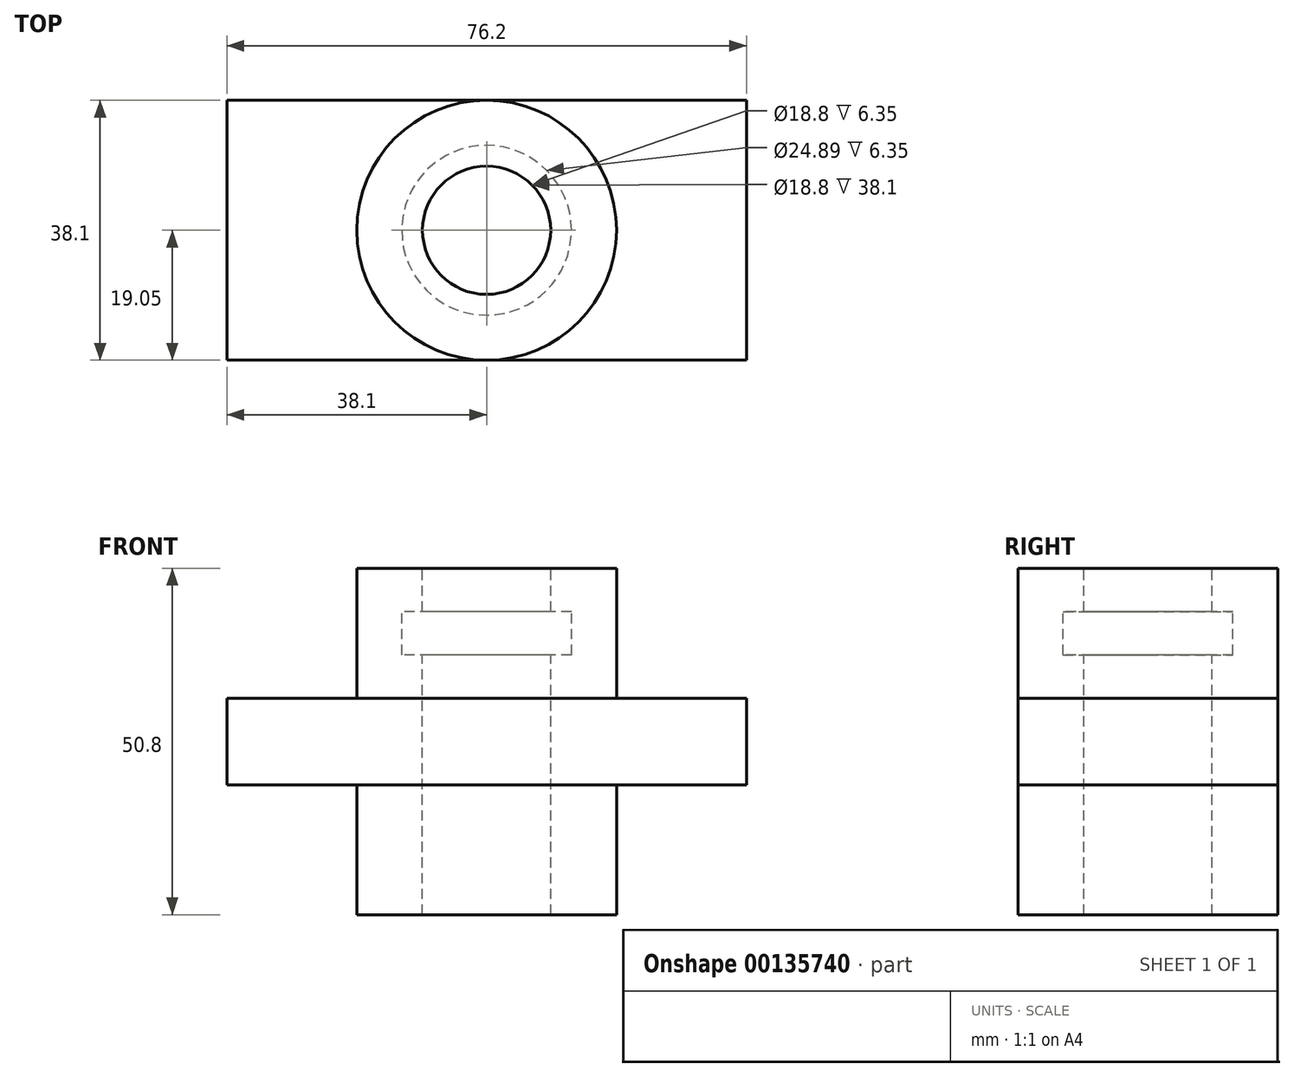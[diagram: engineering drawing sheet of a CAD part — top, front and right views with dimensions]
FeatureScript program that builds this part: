
annotation { "Feature Type Name" : "Feature", "Feature Type Description" : "" }
export const myFeature = defineFeature(function(context is Context, id is Id, definition is map)
    precondition{}
    {
        {
            var Q0;
            Q0=qCreatedBy(makeId("Front.planeOp"),FACE);
            var sketch = newSketch(context, id + "F0", { "sketchPlane" : qUnion([Q0])});
            skLineSegment(sketch, "E0", {"start": v(0, 0) * mm, "end": v(0, 50.8) * mm});
            skLineSegment(sketch, "E1", {"start": v(0, 50.8) * mm, "end": v(-19.05, 50.8) * mm});
            skLineSegment(sketch, "E2", {"start": v(-19.05, 50.8) * mm, "end": v(-19.05, 31.75) * mm});
            skLineSegment(sketch, "E3", {"start": v(-19.05, 31.75) * mm, "end": v(0, 31.75) * mm});
            skLineSegment(sketch, "E4", {"start": v(-19.05, 31.75) * mm, "end": v(-38.1, 31.75) * mm});
            skLineSegment(sketch, "E5", {"start": v(-38.1, 31.75) * mm, "end": v(-38.1, 19.05) * mm});
            skLineSegment(sketch, "E6", {"start": v(-38.1, 19.05) * mm, "end": v(0, 19.05) * mm});
            skLineSegment(sketch, "E7", {"start": v(-19.05, 19.05) * mm, "end": v(-19.05, 0) * mm});
            skLineSegment(sketch, "E8", {"start": v(-19.05, 0) * mm, "end": v(0, 0) * mm});
            skLineSegment(sketch, "E9", {"start": v(-12.45, 44.45) * mm, "end": v(-12.45, 38.1) * mm});
            skLineSegment(sketch, "E10", {"start": v(-12.45, 38.1) * mm, "end": v(-9.4, 38.1) * mm});
            skLineSegment(sketch, "E11", {"start": v(-9.4, 38.1) * mm, "end": v(-9.4, 0) * mm});
            skLineSegment(sketch, "E12", {"start": v(-9.4, 0) * mm, "end": v(0, 0) * mm});
            skLineSegment(sketch, "E13", {"start": v(-9.4, 44.45) * mm, "end": v(-9.4, 50.8) * mm});
            skLineSegment(sketch, "E14", {"start": v(-12.45, 44.45) * mm, "end": v(-9.4, 44.45) * mm});
            skLineSegment(sketch, "E15", {"start": v(0, 0) * mm, "end": v(0, 57.37) * mm, "construction": true});
            skSolve(sketch);
        }
        {
            var Q0;
            Q0 = qSketchRegion(id + "F0", true);
            var Q1;
            Q1=sQuery(id+"F0.wireOp",EDGE,"E0");
            revolve(context, id + "F1", {"entities" : qUnion([Q0]), "axis" : qUnion([Q1]), "revolveType" : RevolveType.FULL});
        }
        {
            var Q0;
            Q0=makeQuery(id+"F1.opRevolve","SWEPT_FACE",FACE,{"disambiguationData":[OSD([sQuery(id+"F0.wireOp",EDGE,"E4")])]});
            var sketch = newSketch(context, id + "F2", { "sketchPlane" : qUnion([Q0])});
            skLineSegment(sketch, "E16.bottom", {"start": v(38.1, 19.05) * mm, "end": v(-38.1, 19.05) * mm});
            skLineSegment(sketch, "E16.top", {"start": v(38.1, -19.05) * mm, "end": v(-38.1, -19.05) * mm});
            skLineSegment(sketch, "E16.left", {"start": v(38.1, 19.05) * mm, "end": v(38.1, -19.05) * mm});
            skLineSegment(sketch, "E16.right", {"start": v(-38.1, 19.05) * mm, "end": v(-38.1, -19.05) * mm});
            skPoint(sketch, "E16.middle", {"position": v(0, 0) * mm});
            skSolve(sketch);
        }
        {
            var Q0;
            {var subQ0=sQuery(id+"F2.wireOp",EDGE,"E16.bottom");var subQ1=sQuery(id+"F0.wireOp",EDGE,"E4");var subQ2=makeQuery(id+"F1.opRevolve","SWEPT_EDGE",EDGE,{"disambiguationData":[OSD([subQ1,sQuery(id+"F0.wireOp",EDGE,"E5")])]});var subQ3=makeQuery(id+"F2.imprint","INTERSECT",VERTEX,{"disambiguationData":[OD(0.0)],"derivedFrom":[subQ2,subQ0]});Q0=makeQuery(id+"F2.imprint","IMPRINT",FACE,{"disambiguationData":[TD([[makeQuery(id+"F2.imprint","IMPRINT",EDGE,{"disambiguationData":[TD([[subQ3,-1.0]])],"derivedFrom":subQ0}),-1.0]])]});}
            var Q1;
            {var subQ0=sQuery(id+"F2.wireOp",EDGE,"E16.top");var subQ1=sQuery(id+"F0.wireOp",EDGE,"E4");var subQ2=makeQuery(id+"F1.opRevolve","SWEPT_EDGE",EDGE,{"disambiguationData":[OSD([subQ1,sQuery(id+"F0.wireOp",EDGE,"E5")])]});var subQ3=makeQuery(id+"F2.imprint","INTERSECT",VERTEX,{"disambiguationData":[OD(0.0)],"derivedFrom":[subQ2,subQ0]});Q1=makeQuery(id+"F2.imprint","IMPRINT",FACE,{"disambiguationData":[TD([[makeQuery(id+"F2.imprint","IMPRINT",EDGE,{"disambiguationData":[TD([[subQ3,-1.0]])],"derivedFrom":subQ0}),1.0]])]});}
            extrude(context, id + "F3", {"entities" : qUnion([Q0, Q1]), "operationType" : NewBodyOperationType.REMOVE, "oppositeDirection" : true, "depth" : 25.4 * mm});
        }
        {
            var Q0;
            Q0=makeQuery(id+"F3.boolean.opBoolean","SPLIT",FACE,{"disambiguationData":[OD(0.0)],"derivedFrom":makeQuery(id+"F1.opRevolve","SWEPT_FACE",FACE,{"disambiguationData":[OSD([sQuery(id+"F0.wireOp",EDGE,"E4")])]})});
            var sketch = newSketch(context, id + "F4", { "sketchPlane" : qUnion([Q0])});
            skArc(sketch, "E17.0.0", {"start": v(-38.1, 0) * mm, "mid": v(-36.8, 9.86) * mm, "end": v(-33, 19.05) * mm});
            skLineSegment(sketch, "E17.0.1", {"start": v(-33, 19.05) * mm, "end": v(-38.1, 19.05) * mm});
            skLineSegment(sketch, "E17.0.2", {"start": v(-38.1, 19.05) * mm, "end": v(-38.1, 0) * mm});
            skLineSegment(sketch, "E18.0.0", {"start": v(-38.1, -19.05) * mm, "end": v(-33, -19.05) * mm});
            skArc(sketch, "E18.0.1", {"start": v(-33, -19.05) * mm, "mid": v(-36.8, -9.86) * mm, "end": v(-38.1, 0) * mm});
            skLineSegment(sketch, "E18.0.2", {"start": v(-38.1, 0) * mm, "end": v(-38.1, -19.05) * mm});
            skLineSegment(sketch, "E19.0.0", {"start": v(38.1, 0) * mm, "end": v(38.1, 19.05) * mm});
            skLineSegment(sketch, "E19.0.1", {"start": v(38.1, 19.05) * mm, "end": v(33, 19.05) * mm});
            skArc(sketch, "E19.0.2", {"start": v(33, 19.05) * mm, "mid": v(36.8, 9.86) * mm, "end": v(38.1, 0) * mm});
            skLineSegment(sketch, "E20.0.0", {"start": v(33, -19.05) * mm, "end": v(38.1, -19.05) * mm});
            skLineSegment(sketch, "E20.0.1", {"start": v(38.1, -19.05) * mm, "end": v(38.1, 0) * mm});
            skArc(sketch, "E20.0.2", {"start": v(38.1, 0) * mm, "mid": v(36.8, -9.86) * mm, "end": v(33, -19.05) * mm});
            skSolve(sketch);
        }
        {
            var Q0;
            Q0 = qSketchRegion(id + "F4", true);
            var Q1;
            Q1=makeQuery(id+"F3.boolean.opBoolean","SPLIT",FACE,{"disambiguationData":[OD(1.0)],"derivedFrom":makeQuery(id+"F1.opRevolve","SWEPT_FACE",FACE,{"disambiguationData":[OSD([sQuery(id+"F0.wireOp",EDGE,"E6")])]})});
            extrude(context, id + "F5", {"entities" : qUnion([Q0]), "operationType" : NewBodyOperationType.ADD, "endBound" : BoundingType.UP_TO_SURFACE, "oppositeDirection" : true, "endBoundEntityFace" : qUnion([Q1]), "depth" : 25.4 * mm});
        }
        {
            var Q0;
            Q0=qCreatedBy(makeId("Front.planeOp"),FACE);
            var sketch = newSketch(context, id + "F6", { "sketchPlane" : qUnion([Q0])});
            skLineSegment(sketch, "E21", {"start": v(-9.4, 50.8) * mm, "end": v(-9.4, 44.45) * mm});
            skLineSegment(sketch, "E22", {"start": v(-9.4, 44.45) * mm, "end": v(-12.45, 44.45) * mm});
            skLineSegment(sketch, "E23", {"start": v(-12.45, 44.45) * mm, "end": v(-12.45, 38.1) * mm});
            skLineSegment(sketch, "E24", {"start": v(-12.45, 38.1) * mm, "end": v(-9.4, 38.1) * mm});
            skLineSegment(sketch, "E25", {"start": v(-9.4, 38.1) * mm, "end": v(-9.4, 0) * mm});
            skLineSegment(sketch, "E26.0", {"start": v(19.05, 0) * mm, "end": v(-19.05, 0) * mm});
            skLineSegment(sketch, "E27.0", {"start": v(19.05, 50.8) * mm, "end": v(-19.05, 50.8) * mm});
            skLineSegment(sketch, "E28", {"start": v(0, 0) * mm, "end": v(0, 50.8) * mm});
            skLineSegment(sketch, "E29", {"start": v(0, 0) * mm, "end": v(0, 50.8) * mm, "construction": true});
            skSolve(sketch);
        }
        {
            var Q0;
            Q0 = qSketchRegion(id + "F6", true);
            var Q1;
            Q1=sQuery(id+"F6.wireOp",EDGE,"E28");
            revolve(context, id + "F7", {"operationType" : NewBodyOperationType.REMOVE, "entities" : qUnion([Q0]), "axis" : qUnion([Q1]), "revolveType" : RevolveType.FULL, "oppositeDirection" : true});
        }
    });
